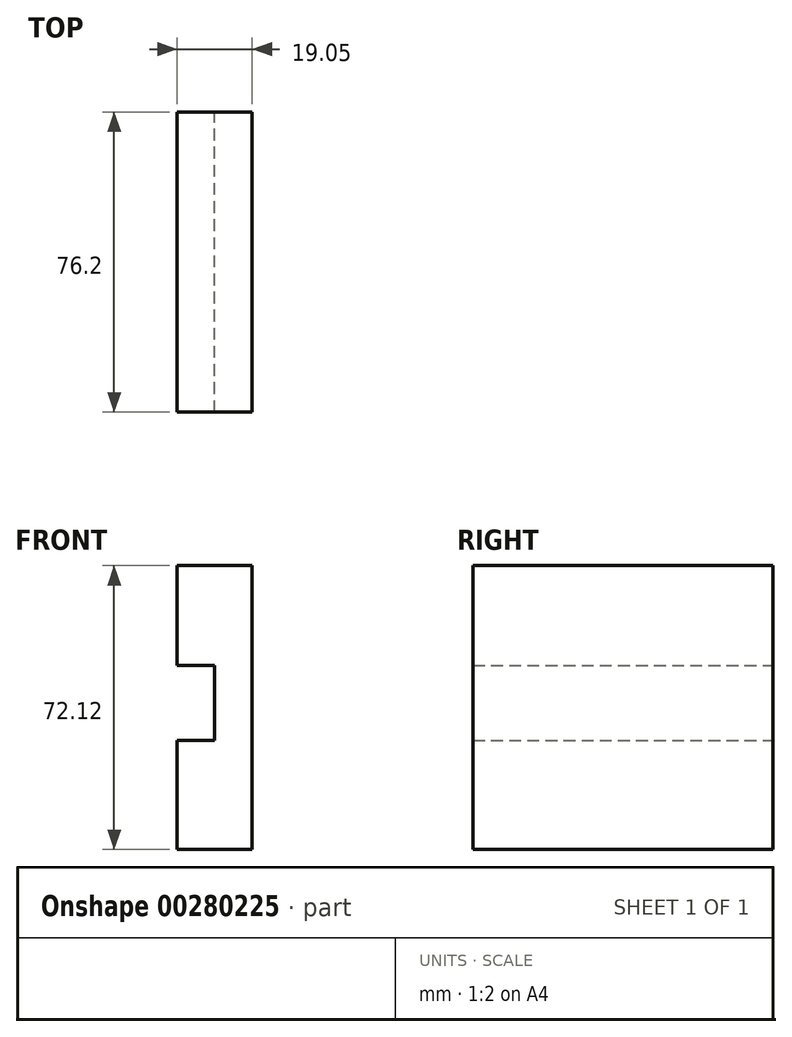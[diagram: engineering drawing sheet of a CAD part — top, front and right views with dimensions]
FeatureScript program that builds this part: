
annotation { "Feature Type Name" : "Feature", "Feature Type Description" : "" }
export const myFeature = defineFeature(function(context is Context, id is Id, definition is map)
    precondition{}
    {
        {
            var Q0;
            Q0=qCreatedBy(makeId("Front.planeOp"),FACE);
            var sketch = newSketch(context, id + "F0", { "sketchPlane" : qUnion([Q0])});
            skLineSegment(sketch, "E0", {"start": v(0, 0) * mm, "end": v(0, 72.12) * mm});
            skLineSegment(sketch, "E1", {"start": v(0, 72.12) * mm, "end": v(-19.05, 72.12) * mm});
            skLineSegment(sketch, "E2", {"start": v(-19.05, 72.12) * mm, "end": v(-19.05, 46.72) * mm});
            skLineSegment(sketch, "E3", {"start": v(-19.05, 46.72) * mm, "end": v(-9.52, 46.72) * mm});
            skLineSegment(sketch, "E4", {"start": v(-9.52, 46.72) * mm, "end": v(-9.52, 27.67) * mm});
            skLineSegment(sketch, "E5", {"start": v(-9.52, 27.67) * mm, "end": v(-19.05, 27.67) * mm});
            skLineSegment(sketch, "E6", {"start": v(-19.05, 27.67) * mm, "end": v(-19.05, 0) * mm});
            skLineSegment(sketch, "E7", {"start": v(-19.05, 0) * mm, "end": v(0, 0) * mm});
            skSolve(sketch);
        }
        {
            var Q0;
            Q0 = qSketchRegion(id + "F0", true);
            extrude(context, id + "F1", {"entities" : qUnion([Q0]), "depth" : 76.2 * mm});
        }
    });
